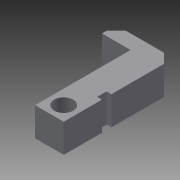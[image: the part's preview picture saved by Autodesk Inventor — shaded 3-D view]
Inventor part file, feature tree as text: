
AUTODESK INVENTOR PART (.ipt)
format: ipt  version: 2015 (Build 190159000, 159)  size: 115,200 bytes
history: native  units: in
note: dims shown in document units (in); Inventor stores cm internally (conversion verified against a paired STEP export)
features: extrude x4, sketch x3, chamfer x1
ambient origin geometry x8: Origin, YZ Plane, XZ Plane, XY Plane, X Axis, Y Axis, Z Axis, Center Point
bodies: Solid1 (feature_tree)
feature tree (8):
  extrude  "Extrusion1"  Depth=0.1969in
  extrude  "Extrusion2"  Depth=0.1181in TaperAngle=0.0deg
  extrude  "Extrusion3"  Depth=0.7874in TaperAngle=0.0deg
  chamfer  "Chamfer1"  Distance=0.1181in
  extrude  "Extrusion4"  Depth=0.1181in
  sketch  "Sketch1"  dims[d0=0.2362in d1=0.1969in]
  sketch  "Sketch2"  dims[d2=0.4724in d3=0.1181in d4=0.0in]
  sketch  "Sketch4"  dims[d5=0.2362in d6=0.7874in d7=0.0in d8=0.1181in d9=0.1181in d10=0.1575in d11=1.1811in d12=0.0in d13=0.0787in d14=0.0787in d15=45.0deg d16=0.0787in d17=0.315in d18=0.0394in d19=0.0in]
